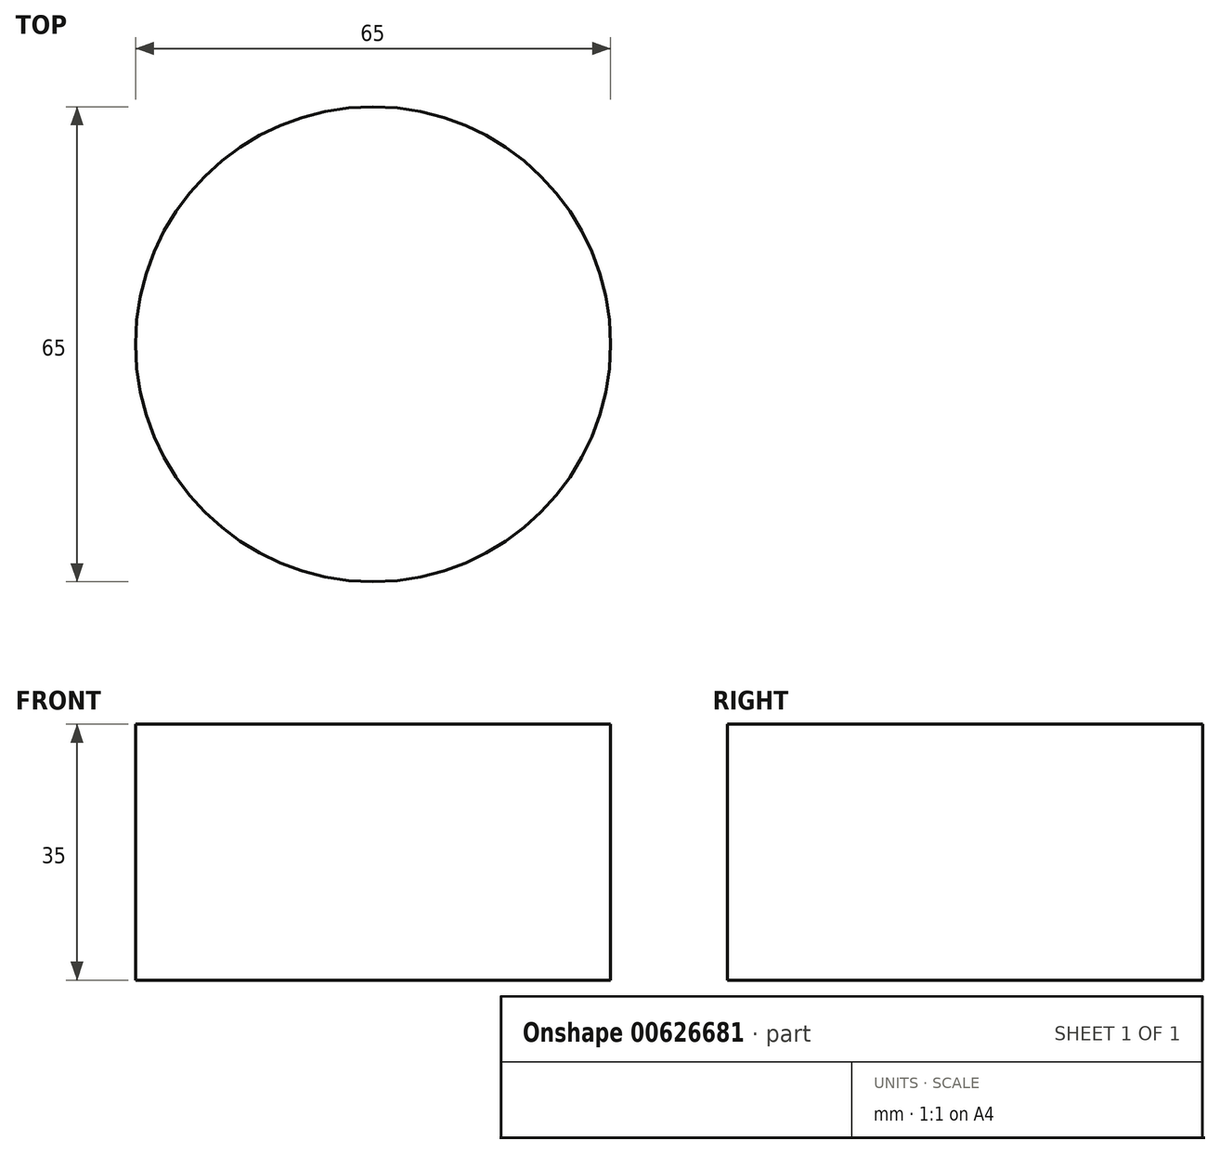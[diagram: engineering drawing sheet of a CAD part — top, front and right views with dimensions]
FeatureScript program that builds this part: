
annotation { "Feature Type Name" : "Feature", "Feature Type Description" : "" }
export const myFeature = defineFeature(function(context is Context, id is Id, definition is map)
    precondition{}
    {
        {
            var Q0;
            Q0=qCreatedBy(makeId("Top.planeOp"),FACE);
            var sketch = newSketch(context, id + "F0", { "sketchPlane" : qUnion([Q0])});
            skCircle(sketch, "E0", {"center": v(-42.86, -22.33) * mm, "radius": 32.5 * mm});
            skSolve(sketch);
        }
        {
            var Q0;
            Q0 = qSketchRegion(id + "F0", true);
            extrude(context, id + "F1", {"entities" : qUnion([Q0]), "depth" : 35 * mm, "offsetDistance" : 25 * mm});
        }
        {
            var Q0;
            Q0=qCreatedBy(makeId("Top.planeOp"),FACE);
            cPlane(context, id + "F2", {"entities" : qUnion([Q0]), "cplaneType" : CPlaneType.OFFSET, "offset" : 5.5 * mm, "width" : 150 * mm, "height" : 150 * mm});
        }
    });
